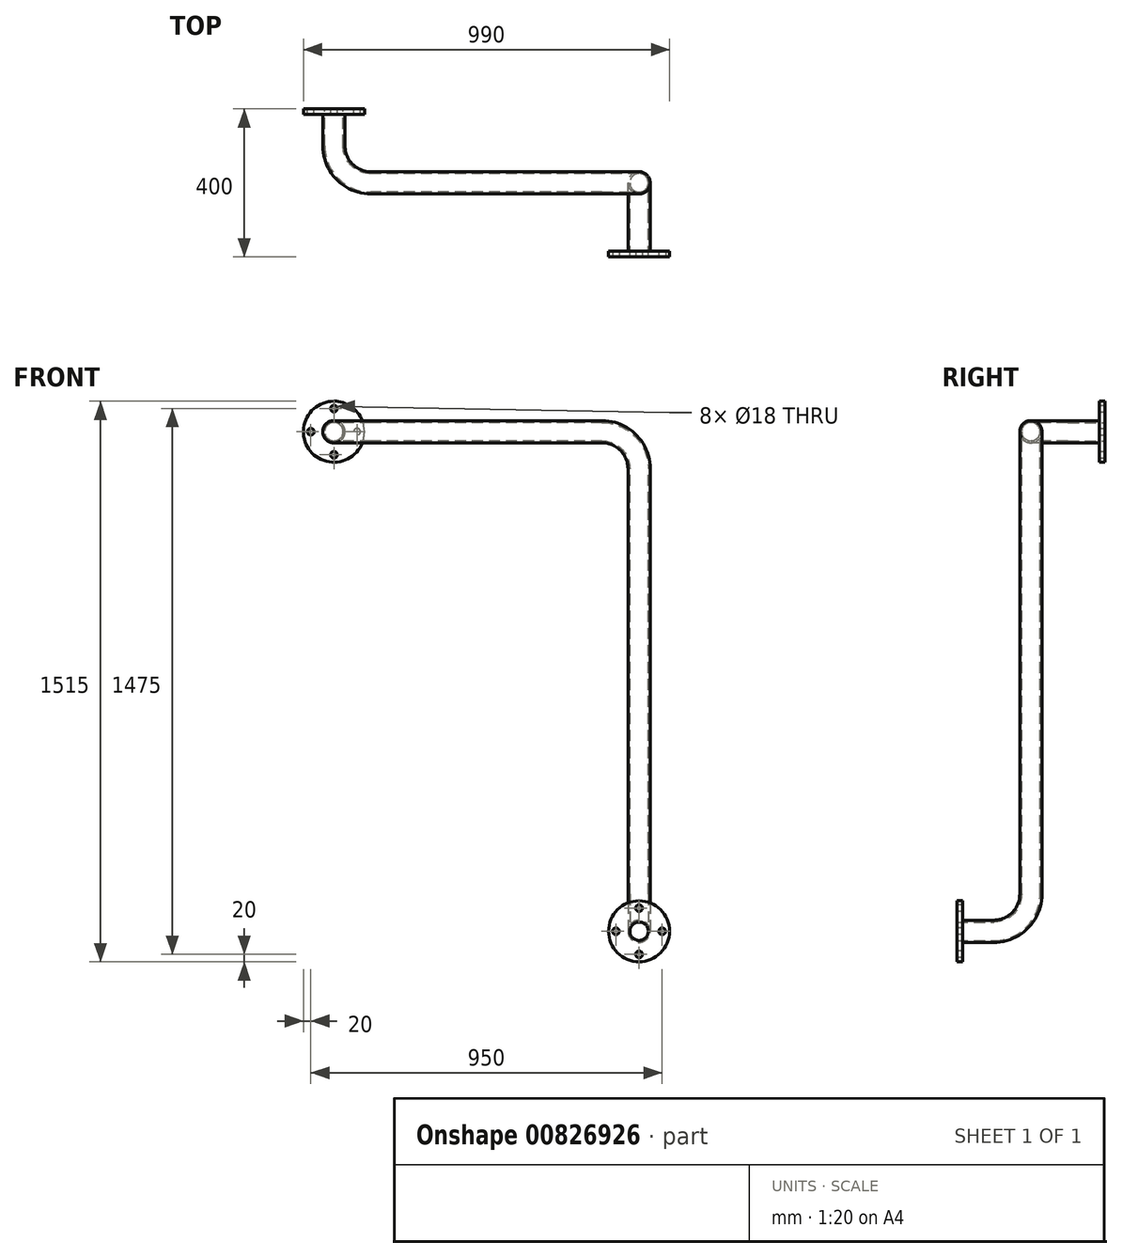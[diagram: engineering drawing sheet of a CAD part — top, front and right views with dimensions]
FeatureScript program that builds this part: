
annotation { "Feature Type Name" : "Feature", "Feature Type Description" : "" }
export const myFeature = defineFeature(function(context is Context, id is Id, definition is map)
    precondition{}
    {
        {
            var Q0;
            Q0=qCreatedBy(makeId("Front.planeOp"),FACE);
            cPlane(context, id + "F0", {"entities" : qUnion([Q0]), "cplaneType" : CPlaneType.OFFSET, "offset" : 200 * mm, "oppositeDirection" : true, "width" : 150 * mm, "height" : 150 * mm});
        }
        {
            var Q0;
            Q0=qCreatedBy(makeId("Right.planeOp"),FACE);
            var sketch = newSketch(context, id + "F1", { "sketchPlane" : qUnion([Q0])});
            skLineSegment(sketch, "E0", {"start": v(0, 0) * mm, "end": v(100, 0) * mm});
            skLineSegment(sketch, "E1", {"start": v(200, 100) * mm, "end": v(200, 1250) * mm});
            skPoint(sketch, "E2.visualSharp", {"position": v(200, 0) * mm});
            skArc(sketch, "E2.filletArc", {"start": v(100, 0) * mm, "mid": v(170.71, 29.29) * mm, "end": v(200, 100) * mm});
            skPoint(sketch, "E3.visualSharp", {"position": v(200, 1350) * mm});
            skLineSegment(sketch, "E4", {"start": v(200, 1250) * mm, "end": v(200, 1350) * mm});
            skSolve(sketch);
        }
        {
            var Q0;
            Q0=qCreatedBy(makeId("Top.planeOp"),FACE);
            cPlane(context, id + "F2", {"entities" : qUnion([Q0]), "cplaneType" : CPlaneType.OFFSET, "offset" : 1350 * mm, "width" : 150 * mm, "height" : 150 * mm});
        }
        {
            var Q0;
            Q0=qCreatedBy(makeId("Front.planeOp"),FACE);
            var sketch = newSketch(context, id + "F3", { "sketchPlane" : qUnion([Q0])});
            skCircle(sketch, "E5", {"center": v(0, 0) * mm, "radius": 25 * mm});
            skCircle(sketch, "E6", {"center": v(0, 0) * mm, "radius": 30 * mm});
            skSolve(sketch);
        }
        {
            var Q0;
            Q0=qCreatedBy(id+"F0.planeOp",FACE);
            var sketch = newSketch(context, id + "F4", { "sketchPlane" : qUnion([Q0])});
            skPoint(sketch, "E7.0", {"position": v(0, 1350) * mm});
            skLineSegment(sketch, "E8.0", {"start": v(0, 1250) * mm, "end": v(0, 1250) * mm});
            skLineSegment(sketch, "E9", {"start": v(-100, 1350) * mm, "end": v(-825, 1350) * mm});
            skArc(sketch, "E10.filletArc", {"start": v(0, 1250) * mm, "mid": v(-29.29, 1320.71) * mm, "end": v(-100, 1350) * mm});
            skSolve(sketch);
        }
        {
            var Q0;
            Q0=qCreatedBy(id+"F2.planeOp",FACE);
            var sketch = newSketch(context, id + "F5", { "sketchPlane" : qUnion([Q0])});
            skLineSegment(sketch, "E11.0", {"start": v(-100, 200) * mm, "end": v(-725, 200) * mm});
            skPoint(sketch, "E12.visualSharp", {"position": v(-825, 200) * mm});
            skLineSegment(sketch, "E13.MirrorCS", {"start": v(-825, 300) * mm, "end": v(-825, 400) * mm});
            skArc(sketch, "E14.MirrorCS", {"start": v(-725, 200) * mm, "mid": v(-795.71, 229.29) * mm, "end": v(-825, 300) * mm});
            skPoint(sketch, "E15.end.orphan", {"position": v(-825, 0) * mm});
            skPoint(sketch, "E12.filletArc.end.orphan", {"position": v(-825, 100) * mm});
            skSolve(sketch);
        }
        {
            var Q0;
            Q0=makeQuery(id+"F3.imprint","IMPRINT",FACE,{"disambiguationData":[TD([[makeQuery(id+"F3.imprint","IMPRINT",EDGE,{"derivedFrom":sQuery(id+"F3.wireOp",EDGE,"E5")}),-1.0]])]});
            var Q1;
            Q1=sQuery(id+"F1.wireOp",EDGE,"E0");
            var Q2;
            Q2=sQuery(id+"F1.wireOp",EDGE,"E2.filletArc");
            var Q3;
            Q3=sQuery(id+"F1.wireOp",EDGE,"E1");
            var Q4;
            Q4=sQuery(id+"F4.wireOp",EDGE,"E10.filletArc");
            var Q5;
            Q5=sQuery(id+"F5.wireOp",EDGE,"E11.0");
            var Q6;
            Q6=sQuery(id+"F5.wireOp",EDGE,"E14.MirrorCS");
            var Q7;
            Q7=sQuery(id+"F5.wireOp",EDGE,"E13.MirrorCS");
            sweep(context, id + "F6", {"profiles" : qUnion([Q0]), "path" : qUnion([Q1, Q2, Q3, Q4, Q5, Q6, Q7])});
        }
        {
            var Q0;
            Q0=makeQuery(id+"F6.opSweep","CAP_FACE",FACE,{"disambiguationData":[OSD([sQuery(id+"F1.wireOp",VERTEX,"E0.start"),sQuery(id+"F3.wireOp",EDGE,"E5"),sQuery(id+"F3.wireOp",EDGE,"E6")])],"isStart":true});
            var sketch = newSketch(context, id + "F7", { "sketchPlane" : qUnion([Q0])});
            skCircle(sketch, "E16", {"center": v(0, 0) * mm, "radius": 82.5 * mm});
            skCircle(sketch, "E17", {"center": v(0, 62.5) * mm, "radius": 9 * mm});
            skCircle(sketch, "E18.1.0", {"center": v(-62.5, 0) * mm, "radius": 9 * mm});
            skCircle(sketch, "E18.2.0", {"center": v(0, -62.5) * mm, "radius": 9 * mm});
            skCircle(sketch, "E18.3.0", {"center": v(62.5, 0) * mm, "radius": 9 * mm});
            skCircle(sketch, "E19.0", {"center": v(0, 0) * mm, "radius": 25 * mm});
            skSolve(sketch);
        }
        {
            var Q0;
            Q0=makeQuery(id+"F7.imprint","IMPRINT",FACE,{"disambiguationData":[TD([[makeQuery(id+"F7.imprint","IMPRINT",EDGE,{"derivedFrom":sQuery(id+"F7.wireOp",EDGE,"E16")}),1.0]])]});
            extrude(context, id + "F8", {"entities" : qUnion([Q0]), "operationType" : NewBodyOperationType.ADD, "oppositeDirection" : true, "depth" : 15 * mm, "offsetDistance" : 25 * mm});
        }
        {
            var Q0;
            Q0=makeQuery(id+"F6.opSweep","CAP_FACE",FACE,{"disambiguationData":[OSD([sQuery(id+"F3.wireOp",EDGE,"E5"),sQuery(id+"F3.wireOp",EDGE,"E6"),sQuery(id+"F5.wireOp",VERTEX,"E15.end")])],"isStart":false});
            var sketch = newSketch(context, id + "F9", { "sketchPlane" : qUnion([Q0])});
            skCircle(sketch, "E20", {"center": v(825, 1350) * mm, "radius": 82.5 * mm});
            skCircle(sketch, "E21", {"center": v(825, 1412.5) * mm, "radius": 9 * mm});
            skCircle(sketch, "E22.1.0", {"center": v(762.5, 1350) * mm, "radius": 9 * mm});
            skCircle(sketch, "E22.2.0", {"center": v(825, 1287.5) * mm, "radius": 9 * mm});
            skCircle(sketch, "E22.3.0", {"center": v(887.5, 1350) * mm, "radius": 9 * mm});
            skCircle(sketch, "E23.0", {"center": v(825, 1350) * mm, "radius": 25 * mm});
            skSolve(sketch);
        }
        {
            var Q0;
            Q0=makeQuery(id+"F9.imprint","IMPRINT",FACE,{"disambiguationData":[TD([[makeQuery(id+"F9.imprint","IMPRINT",EDGE,{"derivedFrom":sQuery(id+"F9.wireOp",EDGE,"E20")}),1.0]])]});
            extrude(context, id + "F10", {"entities" : qUnion([Q0]), "operationType" : NewBodyOperationType.ADD, "oppositeDirection" : true, "depth" : 15 * mm, "offsetDistance" : 25 * mm});
        }
    });
